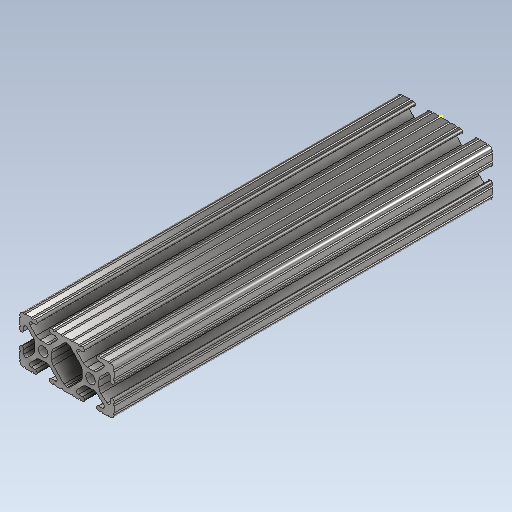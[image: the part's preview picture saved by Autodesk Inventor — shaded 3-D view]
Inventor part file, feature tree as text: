
AUTODESK INVENTOR PART (.ipt)
format: ipt  version: 2020 (Build 240168000, 168)  size: 399,360 bytes
history: native  units: in
note: dims shown in document units (in); Inventor stores cm internally (conversion verified against a paired STEP export)
features: sketch x2, extrude x1
ambient origin geometry x8: Origin, YZ Plane, XZ Plane, XY Plane, X Axis, Y Axis, Z Axis, Center Point
bodies: Solid1 (feature_tree)
feature tree (3):
  extrude  "Extrusion1"  [1 undecoded]
  sketch  "Sketch2"
  sketch  "Sketch1"  dims[d0=8.0in d1=0.0in]
note: 1 required parameter value undecoded (feature->parameter linkage not recoverable at this tier; creation-order binding heuristic only, values carry confidence <= 0.55)
